# Revit family: BVN_BFTX
name_source: partatom
category: Mechanical Equipment
units: mm (PartAtom-declared; Revit-internal decimal feet)

## family parameters
Always vertical = Yes
Cut with Voids When Loaded = No
Host = Wall
Part Type = Normal
Room Calculation Point = No
Round Connector Dimension = Use Diameter
Shared = No

## types (5) — shared parameters
Description = Duct Fan(Wall Type)
Frequency = 50 Hz
Insulation Class = B
Manufacturer = http://www.bahcivanmotor.com.tr
Model = BFTX
Protection Class = 44
URL = http://www.bahcivanmotor.com.tr
Voltage = 230 V
d = 8 mm  [stored 0.0262467 ft]

## per-type parameters (varying)
| type | -f | A | Air Flow | B | BFTX 100 | BFTX 150 | BFTX 200 | BFTX 250 | BFTX 315 | Capacitor | Current | D | F | G | Material Cover | Material Fan | Power | Sound Pressure | Speed(d/d) | Weight | f |
| BFTX 100 | -158 mm | 100 mm  [stored 0.328084 ft] | 270.00 m³/h | 122 mm  [stored 0.400262 ft] | Yes | No | No | No | No | 2 | 0 | 100 mm  [stored 0.328084 ft] | 315 mm  [stored 1.03346 ft] | 265 mm  [stored 0.869423 ft] | Stainless Steel | Stainless Steel | 70 W | 44 | 2900 | 2.70 kg | 158 mm |
| BFTX 150-B | -200 mm  [stored -0.656168 ft] | 150 mm  [stored 0.492126 ft] | 440.00 m³/h | 135 mm  [stored 0.442913 ft] | No | Yes | No | No | No | 2.5 | 0 | 105 mm  [stored 0.344488 ft] | 400 mm  [stored 1.31234 ft] | 350 mm  [stored 1.14829 ft] | <By Category> | <By Category> | 100 W | 46 | 2530 | 3.60 kg | 200 mm  [stored 0.656168 ft] |
| BFTX 200-B | -200 mm  [stored -0.656168 ft] | 200 mm  [stored 0.656168 ft] | 970.00 m³/h | 165 mm | No | No | Yes | No | No | 4 | 1 | 113 mm  [stored 0.370735 ft] | 400 mm  [stored 1.31234 ft] | 350 mm  [stored 1.14829 ft] | <By Category> | <By Category> | 140 W | 48 | 2950 | 4.80 kg | 200 mm  [stored 0.656168 ft] |
| BFTX 250-B | -200 mm  [stored -0.656168 ft] | 250 mm  [stored 0.82021 ft] | 1200.00 m³/h | 165 mm | No | No | No | Yes | No | 6 | 1 | 116 mm  [stored 0.380577 ft] | 400 mm  [stored 1.31234 ft] | 350 mm  [stored 1.14829 ft] | <By Category> | <By Category> | 225 W | 47 | 2675 | 5.30 kg | 200 mm  [stored 0.656168 ft] |
| BFTX 315-B | -250 mm  [stored -0.82021 ft] | 315 mm  [stored 1.03346 ft] | 1890.00 m³/h | 200 mm  [stored 0.656168 ft] | No | No | No | No | Yes | 7 | 1 | 140 mm  [stored 0.459318 ft] | 500 mm  [stored 1.64042 ft] | 400 mm  [stored 1.31234 ft] | <By Category> | <By Category> | 280 W | 49 | 2700 | 6.60 kg | 250 mm  [stored 0.82021 ft] |

note: source unit labels omitted for Current — the stored unit's dimension contradicts the parameter name (converter mislabeling)

note: [stored X ft] marks values corroborated as IEEE doubles in the binary element streams (Revit-internal decimal feet)

## geometry (parser evidence)
native form markers: Sweep x2
no freeform markers — native parametric forms only
